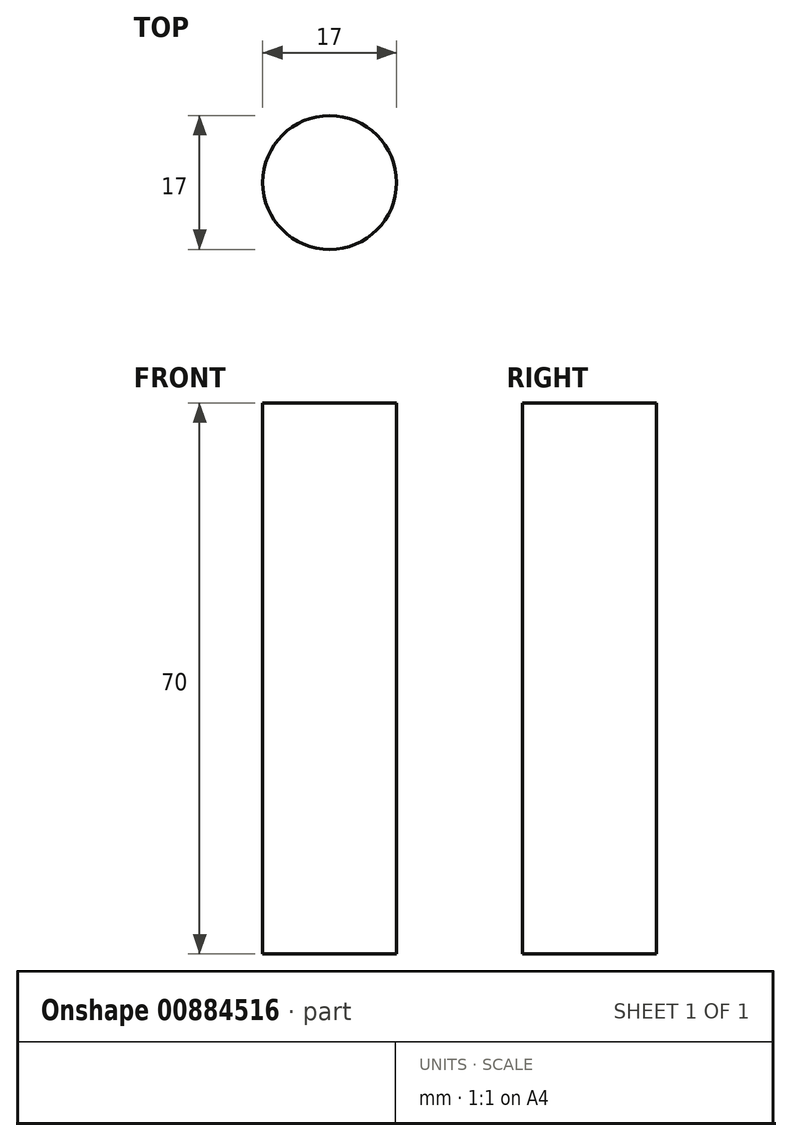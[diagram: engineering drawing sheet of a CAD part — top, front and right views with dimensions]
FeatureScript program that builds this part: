
annotation { "Feature Type Name" : "Feature", "Feature Type Description" : "" }
export const myFeature = defineFeature(function(context is Context, id is Id, definition is map)
    precondition{}
    {
        {
            var Q0;
            Q0=qCreatedBy(makeId("Top.planeOp"),FACE);
            var sketch = newSketch(context, id + "F0", { "sketchPlane" : qUnion([Q0])});
            skCircle(sketch, "E0", {"center": v(0, 0) * mm, "radius": 8.5 * mm});
            skSolve(sketch);
        }
        {
            var Q0;
            Q0=qSketchRegion(id+"F0",true);
            var Q1;
            Q1=makeQuery(id+"F0.imprint","IMPRINT",FACE,{"disambiguationData":[TD([[makeQuery(id+"F0.imprint","IMPRINT",EDGE,{"derivedFrom":sQuery(id+"F0.wireOp",EDGE,"E0")}),1.0]])]});
            extrude(context, id + "F1", {"entities" : qUnion([Q0, Q1]), "depth" : 70 * mm, "offsetDistance" : 25 * mm});
        }
    });
